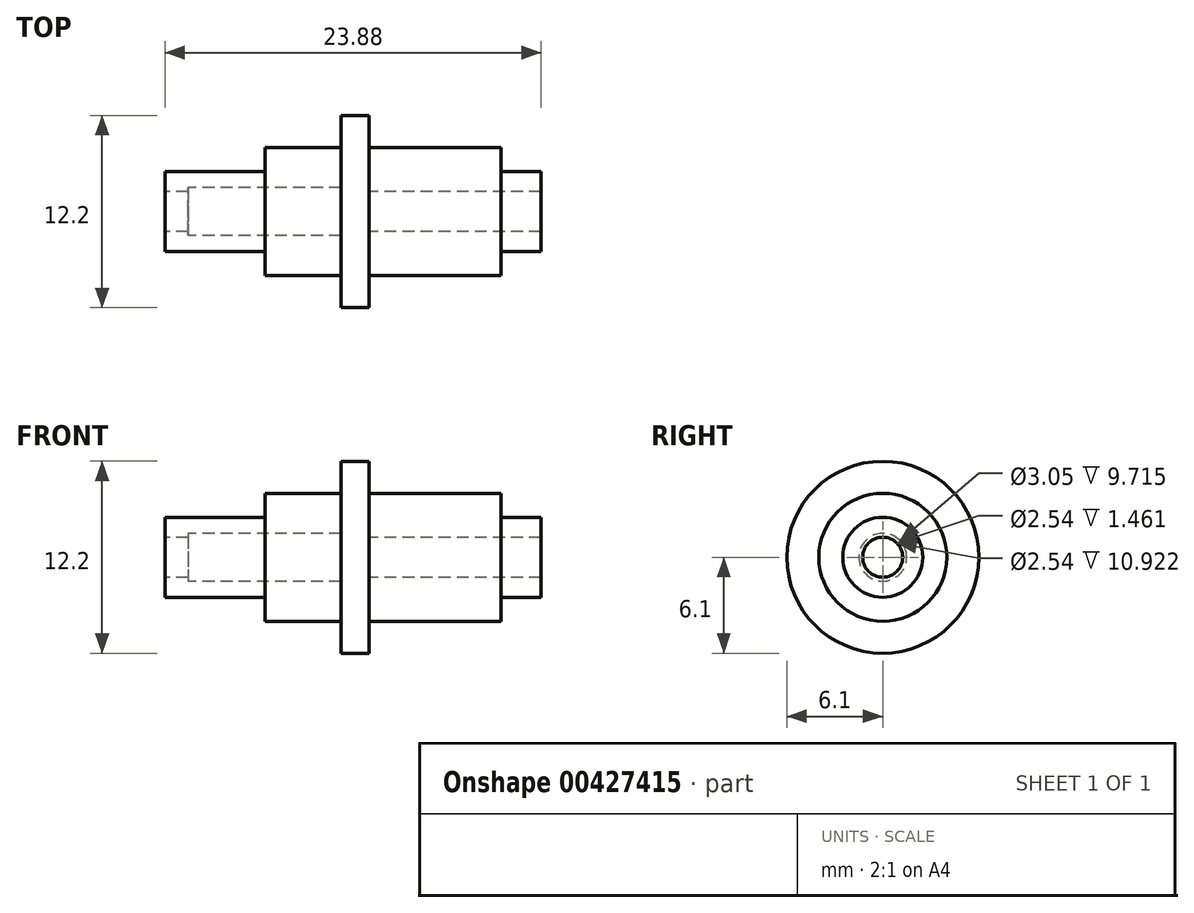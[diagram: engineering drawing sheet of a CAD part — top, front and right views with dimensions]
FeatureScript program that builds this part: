
annotation { "Feature Type Name" : "Feature", "Feature Type Description" : "" }
export const myFeature = defineFeature(function(context is Context, id is Id, definition is map)
    precondition{}
    {
        {
            var Q0;
            Q0=qCreatedBy(makeId("Front.planeOp"),FACE);
            var sketch = newSketch(context, id + "F0", { "sketchPlane" : qUnion([Q0])});
            skLineSegment(sketch, "E0", {"start": v(-10.16, 0) * mm, "end": v(-10.16, 1.27) * mm});
            skLineSegment(sketch, "E1", {"start": v(1.02, 1.27) * mm, "end": v(1.02, 2.54) * mm});
            skLineSegment(sketch, "E2", {"start": v(1.02, 2.54) * mm, "end": v(2.8, 2.54) * mm});
            skLineSegment(sketch, "E3", {"start": v(2.8, 2.54) * mm, "end": v(2.8, 1.27) * mm});
            skLineSegment(sketch, "E4", {"start": v(2.8, 1.27) * mm, "end": v(11.18, 1.27) * mm});
            skLineSegment(sketch, "E5", {"start": v(11.18, 1.27) * mm, "end": v(13.72, 1.27) * mm});
            skLineSegment(sketch, "E6", {"start": v(13.72, 1.27) * mm, "end": v(13.72, 0) * mm});
            skLineSegment(sketch, "E7", {"start": v(13.72, 0) * mm, "end": v(11.18, 0) * mm});
            skLineSegment(sketch, "E8", {"start": v(11.18, 0) * mm, "end": v(11.18, -1.52) * mm});
            skLineSegment(sketch, "E9", {"start": v(11.18, -1.52) * mm, "end": v(2.8, -1.52) * mm});
            skLineSegment(sketch, "E10", {"start": v(2.8, -1.52) * mm, "end": v(2.8, -3.56) * mm});
            skLineSegment(sketch, "E11", {"start": v(2.8, -3.56) * mm, "end": v(1.02, -3.56) * mm});
            skLineSegment(sketch, "E12", {"start": v(1.02, -3.56) * mm, "end": v(1.02, -1.52) * mm});
            skLineSegment(sketch, "E13", {"start": v(1.02, -1.52) * mm, "end": v(-3.8, -1.52) * mm});
            skLineSegment(sketch, "E14", {"start": v(-3.8, -1.52) * mm, "end": v(-3.8, 0) * mm});
            skLineSegment(sketch, "E15", {"start": v(-3.8, 0) * mm, "end": v(-10.16, 0) * mm});
            skLineSegment(sketch, "E16", {"start": v(-10.16, 1.27) * mm, "end": v(-8.7, 1.27) * mm});
            skLineSegment(sketch, "E17", {"start": v(-8.7, 1.27) * mm, "end": v(-8.7, 1.02) * mm});
            skLineSegment(sketch, "E18", {"start": v(-8.7, 1.02) * mm, "end": v(1.02, 1.02) * mm});
            skLineSegment(sketch, "E19", {"start": v(1.02, 1.27) * mm, "end": v(1.02, 1.02) * mm});
            skSolve(sketch);
        }
        {
            var Q0;
            Q0=makeQuery(id+"F0.imprint","IMPRINT",FACE,{"disambiguationData":[TD([[makeQuery(id+"F0.imprint","IMPRINT",EDGE,{"derivedFrom":sQuery(id+"F0.wireOp",EDGE,"E0")}),-1.0]])]});
            var Q1;
            Q1=sQuery(id+"F0.wireOp",EDGE,"E2");
            revolve(context, id + "F1", {"entities" : qUnion([Q0]), "axis" : qUnion([Q1]), "revolveType" : RevolveType.FULL});
        }
    });
